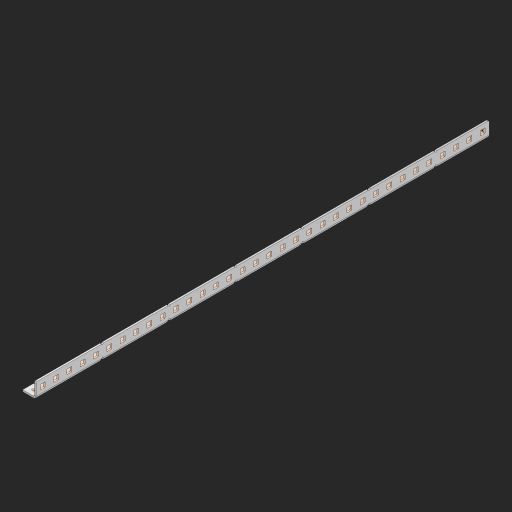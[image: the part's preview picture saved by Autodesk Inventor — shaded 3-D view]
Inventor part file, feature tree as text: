
AUTODESK INVENTOR PART (.ipt)
format: ipt  version: 2023 (Build 270158000, 158)  size: 1,360,896 bytes
history: native  units: in
note: dims shown in document units (in); Inventor stores cm internally (conversion verified against a paired STEP export)
features: other x250, extrude x100, sheet_metal_op x11, sketch x10, pattern_linear x2, mirror x1, chamfer x1
ambient origin geometry x8: Origin, YZ Plane, XZ Plane, XY Plane, X Axis, Y Axis, Z Axis, Center Point
bodies: Solid1 (feature_tree), Body (feature_tree)
feature tree (375):
  other  "Alu Half C 1x2x1x34"
  other  "Table"
  other  "Alu C 1x2x1x35"
  other  "Alu C 1x2x1x34"
  other  "Alu C 1x2x1x33"
  other  "Alu C 1x2x1x32"
  other  "Alu C 1x2x1x31"
  other  "Alu C 1x2x1x30"
  other  "Alu C 1x2x1x29"
  other  "Alu C 1x2x1x28"
  other  "Alu C 1x2x1x27"
  other  "Alu C 1x2x1x26"
  other  "Alu C 1x2x1x25"
  other  "Alu C 1x2x1x24"
  other  "Alu C 1x2x1x23"
  other  "Alu C 1x2x1x22"
  other  "Alu C 1x2x1x21"
  other  "Alu C 1x2x1x20"
  other  "Alu C 1x2x1x19"
  other  "Alu C 1x2x1x18"
  other  "Alu C 1x2x1x17"
  other  "Alu C 1x2x1x16"
  other  "Alu C 1x2x1x15"
  other  "Alu C 1x2x1x14"
  other  "Alu C 1x2x1x13"
  other  "Alu C 1x2x1x12"
  other  "Alu C 1x2x1x11"
  other  "Alu C 1x2x1x10"
  other  "Alu C 1x2x1x9"
  other  "Alu C 1x2x1x8"
  other  "Alu C 1x2x1x7"
  other  "Alu C 1x2x1x6"
  other  "Alu C 1x2x1x5"
  other  "Alu C 1x2x1x4"
  other  "Alu C 1x2x1x3"
  other  "Alu C 1x2x1x2"
  other  "Alu C 1x2x1x1"
  other  "Steel C 1x2x1x35"
  other  "Steel C 1x2x1x34"
  other  "Steel C 1x2x1x33"
  other  "Steel C 1x2x1x32"
  other  "Steel C 1x2x1x31"
  other  "Steel C 1x2x1x30"
  other  "Steel C 1x2x1x29"
  other  "Steel C 1x2x1x28"
  other  "Steel C 1x2x1x27"
  other  "Steel C 1x2x1x26"
  other  "Steel C 1x2x1x25"
  other  "Steel C 1x2x1x24"
  other  "Steel C 1x2x1x23"
  other  "Steel C 1x2x1x22"
  other  "Steel C 1x2x1x21"
  other  "Steel C 1x2x1x20"
  other  "Steel C 1x2x1x19"
  other  "Steel C 1x2x1x18"
  other  "Steel C 1x2x1x17"
  other  "Steel C 1x2x1x16"
  other  "Steel C 1x2x1x15"
  other  "Steel C 1x2x1x14"
  other  "Steel C 1x2x1x13"
  other  "Steel C 1x2x1x12"
  other  "Steel C 1x2x1x11"
  other  "Steel C 1x2x1x10"
  other  "Steel C 1x2x1x9"
  other  "Steel C 1x2x1x8"
  other  "Steel C 1x2x1x7"
  other  "Steel C 1x2x1x6"
  other  "Steel C 1x2x1x5"
  other  "Steel C 1x2x1x4"
  other  "Steel C 1x2x1x3"
  other  "Steel C 1x2x1x2"
  other  "Steel C 1x2x1x1"
  other  "Alu Half C 1x2x1x35"
  other  "Alu Half C 1x2x1x33"
  other  "Alu Half C 1x2x1x32"
  other  "Alu Half C 1x2x1x31"
  other  "Alu Half C 1x2x1x30"
  other  "Alu Half C 1x2x1x29"
  other  "Alu Half C 1x2x1x28"
  other  "Alu Half C 1x2x1x27"
  other  "Alu Half C 1x2x1x26"
  other  "Alu Half C 1x2x1x25"
  other  "Alu Half C 1x2x1x24"
  other  "Alu Half C 1x2x1x23"
  other  "Alu Half C 1x2x1x22"
  other  "Alu Half C 1x2x1x21"
  other  "Alu Half C 1x2x1x20"
  other  "Alu Half C 1x2x1x19"
  other  "Alu Half C 1x2x1x18"
  other  "Alu Half C 1x2x1x17"
  other  "Alu Half C 1x2x1x16"
  other  "Alu Half C 1x2x1x15"
  other  "Alu Half C 1x2x1x14"
  other  "Alu Half C 1x2x1x13"
  other  "Alu Half C 1x2x1x12"
  other  "Alu Half C 1x2x1x11"
  other  "Alu Half C 1x2x1x10"
  other  "Alu Half C 1x2x1x9"
  other  "Alu Half C 1x2x1x8"
  other  "Alu Half C 1x2x1x7"
  other  "Alu Half C 1x2x1x6"
  other  "Alu Half C 1x2x1x5"
  other  "Alu Half C 1x2x1x4"
  other  "Alu Half C 1x2x1x3"
  other  "Alu Half C 1x2x1x2"
  other  "Alu Half C 1x2x1x1"
  other  "Steel Half C 1x2x1x35"
  other  "Steel Half C 1x2x1x34"
  other  "Steel Half C 1x2x1x33"
  other  "Steel Half C 1x2x1x32"
  other  "Steel Half C 1x2x1x31"
  other  "Steel Half C 1x2x1x30"
  other  "Steel Half C 1x2x1x29"
  other  "Steel Half C 1x2x1x28"
  other  "Steel Half C 1x2x1x27"
  other  "Steel Half C 1x2x1x26"
  other  "Steel Half C 1x2x1x25"
  other  "Steel Half C 1x2x1x24"
  other  "Steel Half C 1x2x1x23"
  other  "Steel Half C 1x2x1x22"
  other  "Steel Half C 1x2x1x21"
  other  "Steel Half C 1x2x1x20"
  other  "Steel Half C 1x2x1x19"
  other  "Steel Half C 1x2x1x18"
  other  "Steel Half C 1x2x1x17"
  other  "Steel Half C 1x2x1x16"
  other  "Steel Half C 1x2x1x15"
  other  "Steel Half C 1x2x1x14"
  other  "Steel Half C 1x2x1x13"
  other  "Steel Half C 1x2x1x12"
  other  "Steel Half C 1x2x1x11"
  other  "Steel Half C 1x2x1x10"
  other  "Steel Half C 1x2x1x9"
  other  "Steel Half C 1x2x1x8"
  other  "Steel Half C 1x2x1x7"
  other  "Steel Half C 1x2x1x6"
  other  "Steel Half C 1x2x1x5"
  other  "Steel Half C 1x2x1x4"
  other  "Steel Half C 1x2x1x3"
  other  "Steel Half C 1x2x1x2"
  other  "Steel Half C 1x2x1x1"
  sheet_metal_op  "Flanges"
  other  "Flange Pattern Plane"
  other  "Flange Pattern Sketch"
  sheet_metal_op  "Flange Pattern"
  sheet_metal_op  "Body Pattern"
  pattern_linear  "Center Pattern"  Spacing1=0.0625in  [1 undecoded]
  other  "Arc Length"
  mirror  "Notch Mirror"
  pattern_linear  "Notch Pattern"  Spacing1=0.182in  [1 undecoded]
  chamfer  "End Chamfer"
  extrude  "Half Cut"  Depth=0.02in
  sketch  "Sketch1"  dims[d0=1.0in]
  other  "Plate1"
  sketch  "Sketch2"  dims[d1=17.0in]
  other  "Plate2"
  sheet_metal_op  "Bend1"
  sheet_metal_op  "Corner1"
  sketch  "Sketch3"  dims[d2=0.0625in]
  sketch  "Sketch7"  dims[d3=0.0625in]
  other  "Srf1"
  other  "Srf2"
  sketch  "Sketch8"  dims[d4=0.0312in]
  sketch  "Sketch9"  dims[d5=0.125in]
  other  "Srf91"
  sheet_metal_op  "Body Pattern Sketch"
  other  "Srf92"
  sketch  "Sketch13"  dims[d6=0.0625in]
  sketch  "Sketch14"  dims[d7=0.5in d8=90.0deg d9=0.0312in]
  sketch  "Sketch15"  dims[d10=0.25in]
  sketch  "Sketch16"  dims[d11=0.0625in d12=0.0625in d16=0.182in d17=0.02in d18=0.0625in d19=0.0in d20=0.25in d21=0.25in d38=13.3858in d40=0.5in d41=0.3937in d43=1.0in d46=0.172in d47=1.0in d48=0.0in d49=0.182in d50=0.02in d51=0.25in d52=0.25in d53=0.0625in d54=0.0in d55=0.172in d56=1.0in d57=0.0in d58=0.25in d60=13.3858in d62=0.5in d63=0.3937in d65=0.5in d85=0.1473in d86=0.1782in d88=0.04in d89=0.0625in d90=0.0in d91=0.04in d92=0.0491in d95=2.5in d96=0.04in d97=0.25in d98=45.0deg d99=0.25in d100=0.5in d101=0.0in d102=2.497in d106=0.182in d107=0.02in d108=0.5in d109=0.5in d110=0.0625in d111=0.0in d112=0.172in d113=0.5in d114=0.0in d117=0.5in d118=0.5in d119=0.5in]
  other  "Srf786"
  other  "Srf823"
  other  "Srf824"
  other  "Srf825"
  other  "Srf826"
  other  "Srf827"
  other  "Srf828"
  other  "Srf829"
  other  "Srf856"
  other  "Srf857"
  other  "Srf858"
  other  "Srf859"
  other  "Srf860"
  other  "Srf861"
  other  "Srf862"
  other  "Srf889"
  other  "Srf890"
  other  "Srf891"
  other  "Srf892"
  other  "Srf893"
  other  "Srf894"
  other  "Srf895"
  other  "Srf896"
  other  "Srf922"
  other  "Srf923"
  other  "Srf924"
  other  "Srf925"
  other  "Srf926"
  other  "Srf959"
  other  "Srf960"
  other  "Srf961"
  other  "Srf962"
  other  "Srf963"
  other  "Srf996"
  other  "Srf997"
  other  "Srf998"
  other  "Srf999"
  other  "Srf1000"
  other  "Srf1143"
  other  "Srf1144"
  other  "Srf1145"
  other  "Srf1146"
  other  "Srf1147"
  other  "Srf1148"
  other  "Srf1149"
  other  "Srf1150"
  other  "Srf1151"
  other  "Srf1152"
  other  "Srf1153"
  other  "Srf1154"
  other  "Srf1155"
  other  "Srf1156"
  other  "Srf1157"
  other  "Srf1158"
  other  "Srf1159"
  other  "Srf1160"
  other  "Srf1161"
  other  "Srf1162"
  other  "Srf1199"
  other  "Srf1200"
  other  "Srf1201"
  other  "Srf1202"
  other  "Srf1203"
  other  "Srf1204"
  other  "Srf1205"
  other  "Srf1206"
  other  "Srf1207"
  other  "Srf1208"
  other  "Srf1209"
  other  "Srf1210"
  other  "Srf1211"
  other  "Srf1212"
  other  "Srf1213"
  other  "Srf1214"
  other  "Srf1215"
  other  "Srf1216"
  other  "Srf1217"
  other  "Srf1218"
  other  "Srf1255"
  other  "Srf1256"
  other  "Srf1257"
  other  "Srf1258"
  other  "Srf1259"
  other  "Srf1260"
  other  "Srf1261"
  other  "Srf1262"
  other  "Srf1263"
  other  "Srf1264"
  other  "Srf1265"
  other  "Srf1266"
  other  "Srf1267"
  other  "Srf1268"
  other  "Srf1269"
  other  "Srf1270"
  other  "Srf1271"
  other  "Srf1272"
  other  "Srf1273"
  other  "Srf1274"
  sheet_metal_op  "Flange Stamp"
  sheet_metal_op  "Flange Circle"
  sheet_metal_op  "Body Stamp"
  sheet_metal_op  "Body Circle"
  other  "Center Stamp"
  other  "Center Circle"
  sheet_metal_op  "Notch"
  extrude  "ExtrusionSrf2"  Depth=0.0625in
  extrude  "ExtrusionSrf92"  TaperAngle=0.0deg  [1 undecoded]
  extrude  "ExtrusionSrf823"  Depth=0.25in
  extrude  "ExtrusionSrf824"  Depth=0.25in
  extrude  "ExtrusionSrf825"  Depth=0.5in
  extrude  "ExtrusionSrf826"  Depth=0.5in
  extrude  "ExtrusionSrf827"  Depth=1.0in TaperAngle=0.0deg
  extrude  "ExtrusionSrf828"  Depth=0.182in
  extrude  "ExtrusionSrf829"  Depth=0.02in
  extrude  "ExtrusionSrf856"  Depth=0.25in
  extrude  "ExtrusionSrf857"  Depth=0.25in
  extrude  "ExtrusionSrf858"  Depth=0.0625in
  extrude  "ExtrusionSrf859"  TaperAngle=0.0deg  [1 undecoded]
  extrude  "ExtrusionSrf860"  Depth=0.5in
  extrude  "ExtrusionSrf861"  Depth=1.0in TaperAngle=0.0deg
  extrude  "ExtrusionSrf862"  Depth=0.25in
  extrude  "ExtrusionSrf889"  Depth=0.5in
  extrude  "ExtrusionSrf890"  Depth=0.5in
  extrude  "ExtrusionSrf891"  Depth=0.5in
  extrude  "ExtrusionSrf892"  Depth=0.5in
  extrude  "ExtrusionSrf893"  Depth=0.5in
  extrude  "ExtrusionSrf894"  Depth=0.0625in
  extrude  "ExtrusionSrf895"  TaperAngle=0.0deg  [1 undecoded]
  extrude  "ExtrusionSrf896"  Depth=0.5in
  extrude  "ExtrusionSrf922"  Depth=0.5in
  extrude  "ExtrusionSrf923"  Depth=2.5in
  extrude  "ExtrusionSrf924"  Depth=0.25in TaperAngle=45.0deg
  extrude  "ExtrusionSrf925"  Depth=0.25in
  extrude  "ExtrusionSrf926"  Depth=0.5in TaperAngle=0.0deg
  extrude  "ExtrusionSrf959"  Depth=0.5in
  extrude  "ExtrusionSrf960"  Depth=0.182in
  extrude  "ExtrusionSrf961"  Depth=0.02in
  extrude  "ExtrusionSrf962"  Depth=0.5in
  extrude  "ExtrusionSrf963"  Depth=0.5in
  extrude  "ExtrusionSrf996"  Depth=0.0625in
  extrude  "ExtrusionSrf997"  TaperAngle=0.0deg  [1 undecoded]
  extrude  "ExtrusionSrf998"  Depth=0.5in
  extrude  "ExtrusionSrf999"  Depth=0.5in TaperAngle=0.0deg
  extrude  "ExtrusionSrf1000"  Depth=0.5in
  extrude  "ExtrusionSrf1143"  Depth=0.5in
  extrude  "ExtrusionSrf1144"  Depth=0.5in
  extrude  "ExtrusionSrf1145"  [1 undecoded]
  extrude  "ExtrusionSrf1146"  [1 undecoded]
  extrude  "ExtrusionSrf1147"  [1 undecoded]
  extrude  "ExtrusionSrf1148"  [1 undecoded]
  extrude  "ExtrusionSrf1149"  [1 undecoded]
  extrude  "ExtrusionSrf1150"  [1 undecoded]
  extrude  "ExtrusionSrf1151"  [1 undecoded]
  extrude  "ExtrusionSrf1152"  [1 undecoded]
  extrude  "ExtrusionSrf1153"  [1 undecoded]
  extrude  "ExtrusionSrf1154"  [1 undecoded]
  extrude  "ExtrusionSrf1155"  [1 undecoded]
  extrude  "ExtrusionSrf1156"  [1 undecoded]
  extrude  "ExtrusionSrf1157"  [1 undecoded]
  extrude  "ExtrusionSrf1158"  [1 undecoded]
  extrude  "ExtrusionSrf1159"  [1 undecoded]
  extrude  "ExtrusionSrf1160"  [1 undecoded]
  extrude  "ExtrusionSrf1161"  [1 undecoded]
  extrude  "ExtrusionSrf1162"  [1 undecoded]
  extrude  "ExtrusionSrf1199"  [1 undecoded]
  extrude  "ExtrusionSrf1200"  [1 undecoded]
  extrude  "ExtrusionSrf1201"  [1 undecoded]
  extrude  "ExtrusionSrf1202"  [1 undecoded]
  extrude  "ExtrusionSrf1203"  [1 undecoded]
  extrude  "ExtrusionSrf1204"  [1 undecoded]
  extrude  "ExtrusionSrf1205"  [1 undecoded]
  extrude  "ExtrusionSrf1206"  [1 undecoded]
  extrude  "ExtrusionSrf1207"  [1 undecoded]
  extrude  "ExtrusionSrf1208"  [1 undecoded]
  extrude  "ExtrusionSrf1209"  [1 undecoded]
  extrude  "ExtrusionSrf1210"  [1 undecoded]
  extrude  "ExtrusionSrf1211"  [1 undecoded]
  extrude  "ExtrusionSrf1212"  [1 undecoded]
  extrude  "ExtrusionSrf1213"  [1 undecoded]
  extrude  "ExtrusionSrf1214"  [1 undecoded]
  extrude  "ExtrusionSrf1215"  [1 undecoded]
  extrude  "ExtrusionSrf1216"  [1 undecoded]
  extrude  "ExtrusionSrf1217"  [1 undecoded]
  extrude  "ExtrusionSrf1218"  [1 undecoded]
  extrude  "ExtrusionSrf1255"  [1 undecoded]
  extrude  "ExtrusionSrf1256"  [1 undecoded]
  extrude  "ExtrusionSrf1257"  [1 undecoded]
  extrude  "ExtrusionSrf1258"  [1 undecoded]
  extrude  "ExtrusionSrf1259"  [1 undecoded]
  extrude  "ExtrusionSrf1260"  [1 undecoded]
  extrude  "ExtrusionSrf1261"  [1 undecoded]
  extrude  "ExtrusionSrf1262"  [1 undecoded]
  extrude  "ExtrusionSrf1263"  [1 undecoded]
  extrude  "ExtrusionSrf1264"  [1 undecoded]
  extrude  "ExtrusionSrf1265"  [1 undecoded]
  extrude  "ExtrusionSrf1266"  [1 undecoded]
  extrude  "ExtrusionSrf1267"  [1 undecoded]
  extrude  "ExtrusionSrf1268"  [1 undecoded]
  extrude  "ExtrusionSrf1269"  [1 undecoded]
  extrude  "ExtrusionSrf1270"  [1 undecoded]
  extrude  "ExtrusionSrf1271"  [1 undecoded]
  extrude  "ExtrusionSrf1272"  [1 undecoded]
  extrude  "ExtrusionSrf1273"  [1 undecoded]
  extrude  "ExtrusionSrf1274"  [1 undecoded]
note: 64 required parameter values undecoded (feature->parameter linkage not recoverable at this tier; creation-order binding heuristic only, values carry confidence <= 0.55)
